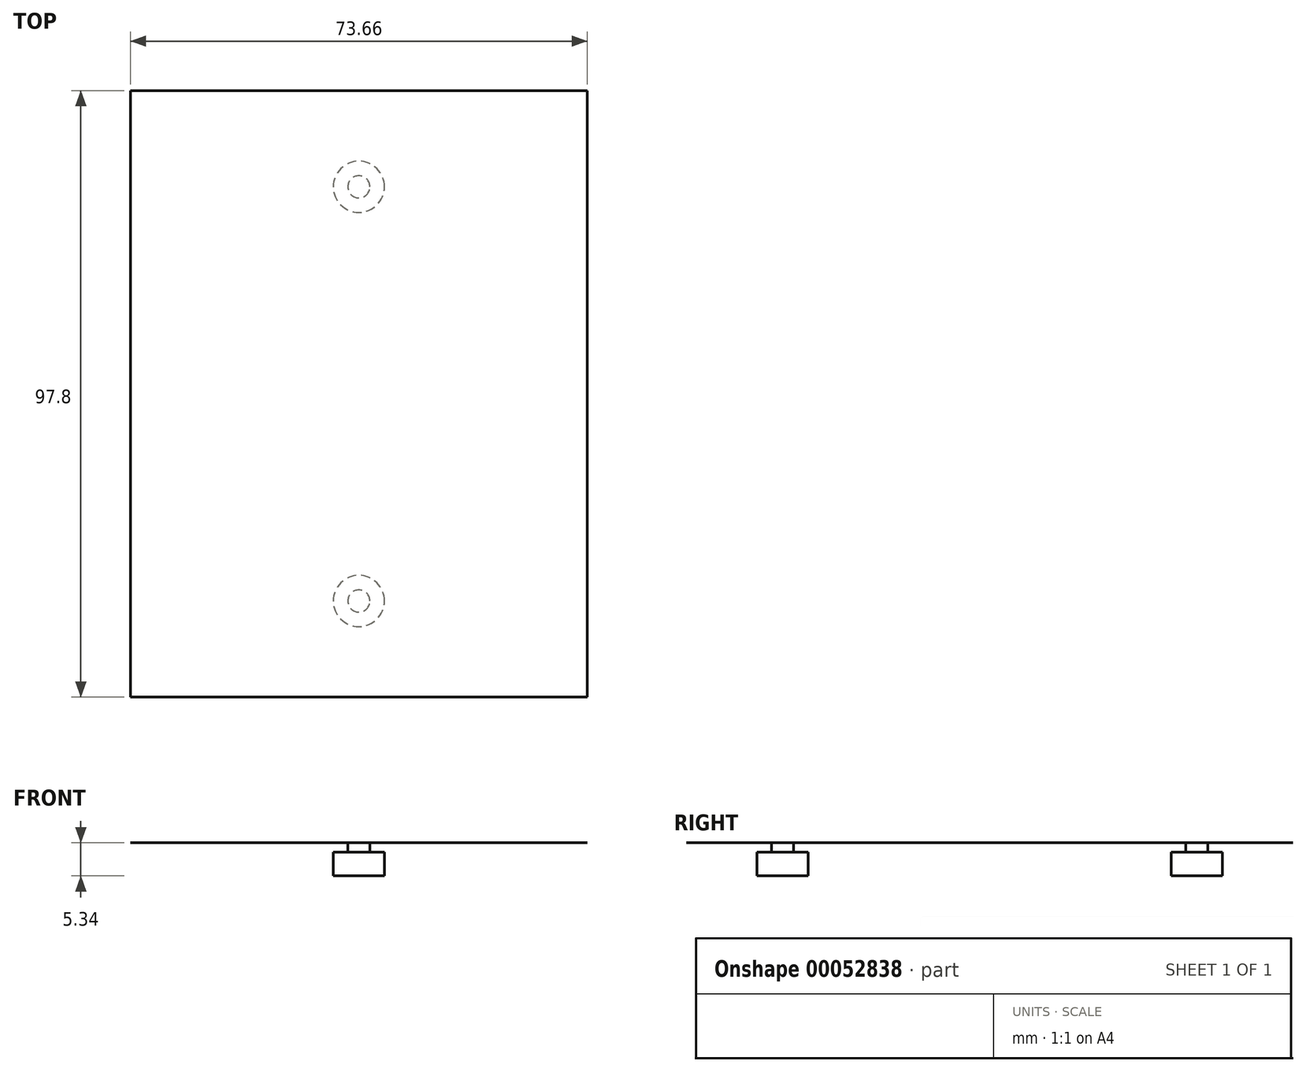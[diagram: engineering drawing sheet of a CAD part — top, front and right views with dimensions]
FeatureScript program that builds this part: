
annotation { "Feature Type Name" : "Feature", "Feature Type Description" : "" }
export const myFeature = defineFeature(function(context is Context, id is Id, definition is map)
    precondition{}
    {
        {
            var Q0;
            Q0=qCreatedBy(makeId("Top.planeOp"),FACE);
            var sketch = newSketch(context, id + "F0", { "sketchPlane" : qUnion([Q0])});
            skLineSegment(sketch, "E0.bottom", {"start": v(-36.83, -48.9) * mm, "end": v(36.83, -48.9) * mm});
            skLineSegment(sketch, "E0.top", {"start": v(-36.83, 48.9) * mm, "end": v(36.83, 48.9) * mm});
            skLineSegment(sketch, "E0.left", {"start": v(-36.83, -48.9) * mm, "end": v(-36.83, 48.9) * mm});
            skLineSegment(sketch, "E0.right", {"start": v(36.83, -48.9) * mm, "end": v(36.83, 48.9) * mm});
            skLineSegment(sketch, "E1", {"start": v(36.83, -48.9) * mm, "end": v(-36.83, 48.9) * mm, "construction": true});
            skLineSegment(sketch, "E2", {"start": v(-36.83, -48.9) * mm, "end": v(36.83, 48.9) * mm, "construction": true});
            skSolve(sketch);
        }
        {
            var Q0;
            Q0=qSketchRegion(id+"F0",true);
            extrude(context, id + "F1", {"entities" : qUnion([Q0]), "depth" : 3 / 203.2 * mm});
        }
        {
            var Q0;
            Q0=qCreatedBy(makeId("Right.planeOp"),FACE);
            var sketch = newSketch(context, id + "F2", { "sketchPlane" : qUnion([Q0])});
            skLineSegment(sketch, "E3", {"start": v(33.4, 0) * mm, "end": v(33.4, -5.33) * mm});
            skLineSegment(sketch, "E4", {"start": v(33.4, -5.33) * mm, "end": v(37.53, -5.33) * mm});
            skLineSegment(sketch, "E5", {"start": v(37.53, -5.33) * mm, "end": v(37.53, -1.52) * mm});
            skLineSegment(sketch, "E6", {"start": v(37.53, -1.52) * mm, "end": v(35.18, -1.52) * mm});
            skLineSegment(sketch, "E7", {"start": v(35.18, -1.52) * mm, "end": v(35.18, 0) * mm});
            skLineSegment(sketch, "E8", {"start": v(35.18, 0) * mm, "end": v(33.4, 0) * mm});
            skLineSegment(sketch, "E9.MirrorCS", {"start": v(-35.18, 0) * mm, "end": v(-33.4, 0) * mm});
            skLineSegment(sketch, "E10.MirrorCS", {"start": v(-35.18, -1.52) * mm, "end": v(-35.18, 0) * mm});
            skLineSegment(sketch, "E11.MirrorCS", {"start": v(-37.53, -1.52) * mm, "end": v(-35.18, -1.52) * mm});
            skLineSegment(sketch, "E12.MirrorCS", {"start": v(-37.53, -5.33) * mm, "end": v(-37.53, -1.52) * mm});
            skLineSegment(sketch, "E13.MirrorCS", {"start": v(-33.4, 0) * mm, "end": v(-33.4, -5.33) * mm});
            skLineSegment(sketch, "E14.MirrorCS", {"start": v(-33.4, -5.33) * mm, "end": v(-37.53, -5.33) * mm});
            skSolve(sketch);
        }
        {
            var Q0;
            Q0=makeQuery(id+"F2.imprint","IMPRINT",FACE,{"disambiguationData":[TD([[makeQuery(id+"F2.imprint","IMPRINT",EDGE,{"derivedFrom":sQuery(id+"F2.wireOp",EDGE,"E3")}),1.0]])]});
            var Q1;
            Q1=sQuery(id+"F2.wireOp",EDGE,"E3");
            revolve(context, id + "F3", {"operationType" : NewBodyOperationType.ADD, "entities" : qUnion([Q0]), "axis" : qUnion([Q1]), "revolveType" : RevolveType.FULL});
        }
        {
            var Q0;
            Q0=makeQuery(id+"F2.imprint","IMPRINT",FACE,{"disambiguationData":[TD([[makeQuery(id+"F2.imprint","IMPRINT",EDGE,{"derivedFrom":sQuery(id+"F2.wireOp",EDGE,"E9.MirrorCS")}),-1.0]])]});
            var Q1;
            Q1=sQuery(id+"F2.wireOp",EDGE,"E13.MirrorCS");
            revolve(context, id + "F4", {"operationType" : NewBodyOperationType.ADD, "entities" : qUnion([Q0]), "axis" : qUnion([Q1]), "revolveType" : RevolveType.FULL});
        }
    });
